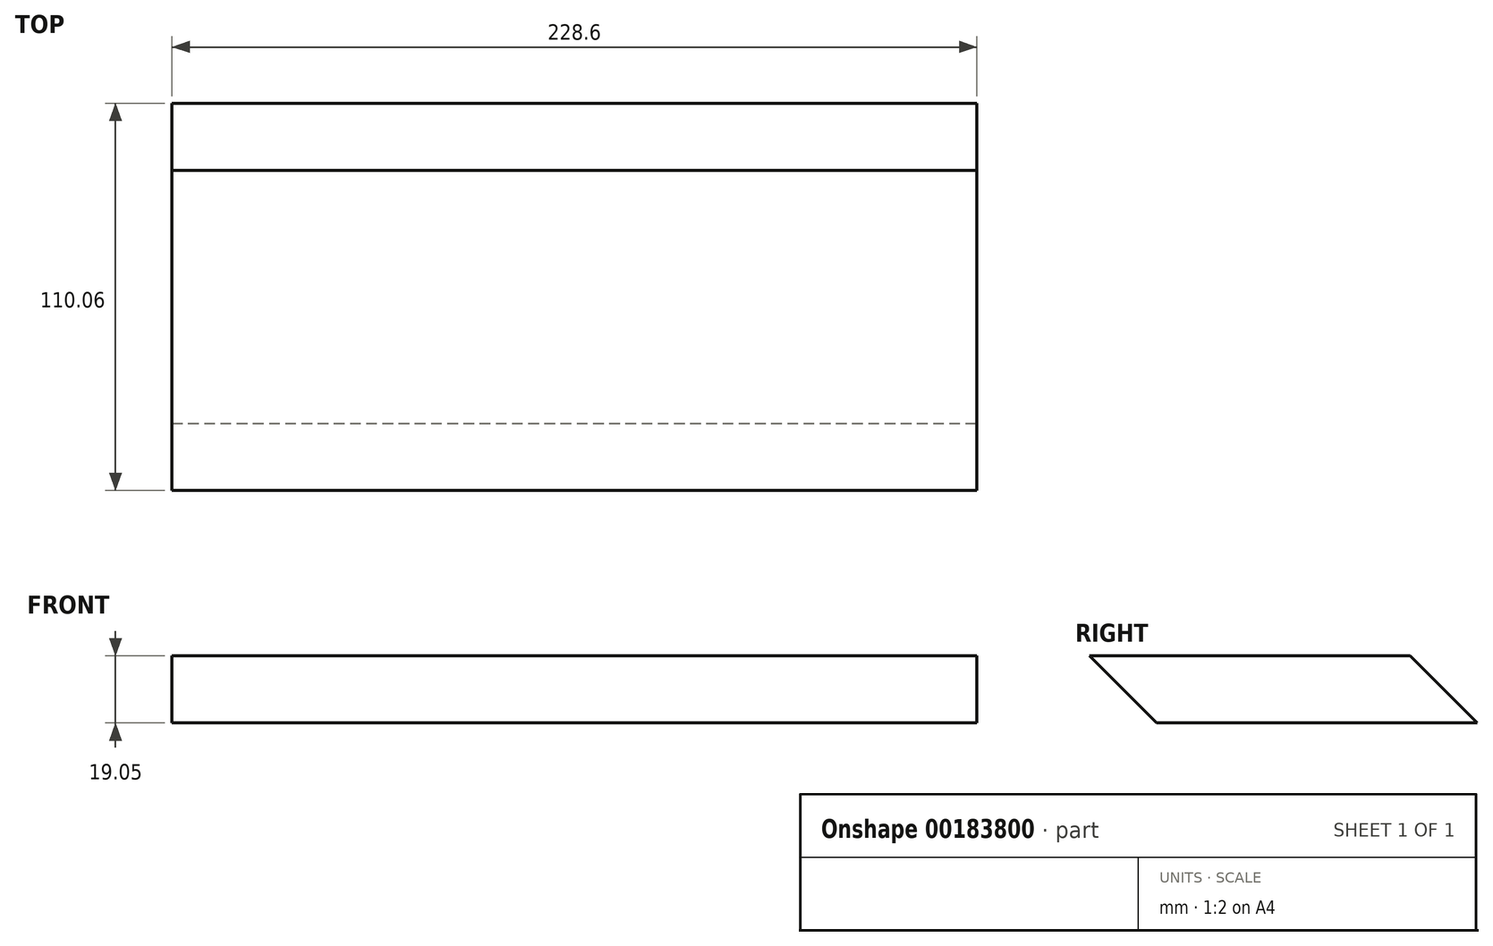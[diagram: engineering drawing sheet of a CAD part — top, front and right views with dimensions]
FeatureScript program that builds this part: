
annotation { "Feature Type Name" : "Feature", "Feature Type Description" : "" }
export const myFeature = defineFeature(function(context is Context, id is Id, definition is map)
    precondition{}
    {
        {
            var Q0;
            Q0=qCreatedBy(makeId("Right.planeOp"),FACE);
            var sketch = newSketch(context, id + "F0", { "sketchPlane" : qUnion([Q0])});
            skLineSegment(sketch, "E0.bottom", {"start": v(0, 0) * mm, "end": v(273.05, 0) * mm});
            skLineSegment(sketch, "E0.top", {"start": v(0, 228.6) * mm, "end": v(273.05, 228.6) * mm});
            skLineSegment(sketch, "E0.left", {"start": v(0, 0) * mm, "end": v(0, 228.6) * mm});
            skLineSegment(sketch, "E0.right", {"start": v(273.05, 0) * mm, "end": v(273.05, 228.6) * mm});
            skSolve(sketch);
        }
        {
            var Q0;
            Q0=qSketchRegion(id+"F0",true);
            extrude(context, id + "F1", {"entities" : qUnion([Q0]), "oppositeDirection" : true, "depth" : 228.6 * mm});
        }
        {
            var Q0;
            Q0=makeQuery(id+"F1.opExtrude","CAP_FACE",FACE,{"disambiguationData":[OSD([sQuery(id+"F0.wireOp",EDGE,"E0.bottom"),sQuery(id+"F0.wireOp",EDGE,"E0.top"),sQuery(id+"F0.wireOp",EDGE,"E0.left"),sQuery(id+"F0.wireOp",EDGE,"E0.right")])],"isStart":true});
            var sketch = newSketch(context, id + "F2", { "sketchPlane" : qUnion([Q0])});
            skLineSegment(sketch, "E1", {"start": v(91.02, 228.6) * mm, "end": v(91.02, 69.85) * mm, "construction": true});
            skLineSegment(sketch, "E2", {"start": v(182.03, 228.6) * mm, "end": v(182.03, 139.7) * mm, "construction": true});
            skLineSegment(sketch, "E3", {"start": v(0, 190.24) * mm, "end": v(91.02, 190.24) * mm, "construction": true});
            skLineSegment(sketch, "E4", {"start": v(91.02, 190.24) * mm, "end": v(182.03, 190.24) * mm, "construction": true});
            skLineSegment(sketch, "E5", {"start": v(182.03, 190.24) * mm, "end": v(273.05, 190.24) * mm, "construction": true});
            skLineSegment(sketch, "E6", {"start": v(273.05, 139.7) * mm, "end": v(182.03, 139.7) * mm});
            skLineSegment(sketch, "E7", {"start": v(273.05, 69.85) * mm, "end": v(91.02, 69.85) * mm});
            skLineSegment(sketch, "E8", {"start": v(40.37, 139.7) * mm, "end": v(40.37, 69.85) * mm, "construction": true});
            skLineSegment(sketch, "E9", {"start": v(40.37, 69.85) * mm, "end": v(40.37, 0) * mm, "construction": true});
            skLineSegment(sketch, "E10", {"start": v(91.02, 69.85) * mm, "end": v(91.02, 0) * mm});
            skLineSegment(sketch, "E11", {"start": v(91.02, 69.85) * mm, "end": v(0, 69.85) * mm, "construction": true});
            skLineSegment(sketch, "E12", {"start": v(182.03, 139.7) * mm, "end": v(182.03, 0) * mm});
            skLineSegment(sketch, "E13", {"start": v(182.03, 139.7) * mm, "end": v(0, 139.7) * mm, "construction": true});
            skSolve(sketch);
        }
        {
            var Q0;
            {var subQ1=sQuery(id+"F2.wireOp",EDGE,"E6");Q0=makeQuery(id+"F2.imprint","IMPRINT",FACE,{"disambiguationData":[TD([[makeQuery(id+"F2.imprint","IMPRINT",EDGE,{"derivedFrom":subQ1}),-1.0]])]});}
            var Q1;
            Q1=makeQuery(id+"F1.opExtrude","CAP_FACE",FACE,{"disambiguationData":[OSD([sQuery(id+"F0.wireOp",EDGE,"E0.bottom"),sQuery(id+"F0.wireOp",EDGE,"E0.top"),sQuery(id+"F0.wireOp",EDGE,"E0.left"),sQuery(id+"F0.wireOp",EDGE,"E0.right")])],"isStart":false});
            extrude(context, id + "F3", {"entities" : qUnion([Q0]), "operationType" : NewBodyOperationType.REMOVE, "endBound" : BoundingType.UP_TO_SURFACE, "oppositeDirection" : true, "endBoundEntityFace" : qUnion([Q1]), "depth" : 25.4 * mm});
        }
        {
            var Q0;
            Q0=makeQuery(id+"F1.opExtrude","CAP_FACE",FACE,{"disambiguationData":[OSD([sQuery(id+"F0.wireOp",EDGE,"E0.bottom"),sQuery(id+"F0.wireOp",EDGE,"E0.top"),sQuery(id+"F0.wireOp",EDGE,"E0.left"),sQuery(id+"F0.wireOp",EDGE,"E0.right")])],"isStart":true});
            var sketch = newSketch(context, id + "F4", { "sketchPlane" : qUnion([Q0])});
            skLineSegment(sketch, "E14.0", {"start": v(110.07, 50.8) * mm, "end": v(110.07, 0) * mm});
            skLineSegment(sketch, "E14.1", {"start": v(201.08, 50.8) * mm, "end": v(110.07, 50.8) * mm});
            skLineSegment(sketch, "E14.2", {"start": v(201.08, 120.65) * mm, "end": v(201.08, 50.8) * mm});
            skLineSegment(sketch, "E14.3", {"start": v(273.05, 120.65) * mm, "end": v(201.08, 120.65) * mm});
            skSolve(sketch);
        }
        {
            var Q0;
            {var subQ1=sQuery(id+"F4.wireOp",EDGE,"E14.0");Q0=makeQuery(id+"F4.imprint","IMPRINT",FACE,{"disambiguationData":[TD([[makeQuery(id+"F4.imprint","IMPRINT",EDGE,{"derivedFrom":subQ1}),1.0]])]});}
            extrude(context, id + "F5", {"entities" : qUnion([Q0]), "operationType" : NewBodyOperationType.REMOVE, "endBound" : BoundingType.UP_TO_NEXT, "oppositeDirection" : true, "depth" : 25.4 * mm});
        }
        {
            var Q0;
            Q0=makeQuery(id+"F1.opExtrude","CAP_FACE",FACE,{"disambiguationData":[OSD([sQuery(id+"F0.wireOp",EDGE,"E0.bottom"),sQuery(id+"F0.wireOp",EDGE,"E0.top"),sQuery(id+"F0.wireOp",EDGE,"E0.left"),sQuery(id+"F0.wireOp",EDGE,"E0.right")])],"isStart":true});
            var sketch = newSketch(context, id + "F6", { "sketchPlane" : qUnion([Q0])});
            skLineSegment(sketch, "E15", {"start": v(91.02, 69.85) * mm, "end": v(110.07, 50.8) * mm});
            skLineSegment(sketch, "E16", {"start": v(182.03, 69.85) * mm, "end": v(201.08, 50.8) * mm});
            skLineSegment(sketch, "E17", {"start": v(182.03, 139.7) * mm, "end": v(201.08, 120.65) * mm});
            skSolve(sketch);
        }
        {
            var Q0;
            Q0=makeQuery(id+"F6.imprint","IMPRINT",FACE,{"disambiguationData":[TD([[makeQuery(id+"F6.imprint","IMPRINT",EDGE,{"derivedFrom":sQuery(id+"F6.wireOp",EDGE,"E17")}),1.0]])]});
            var Q1;
            Q1=makeQuery(id+"F6.imprint","IMPRINT",FACE,{"disambiguationData":[TD([[makeQuery(id+"F6.imprint","IMPRINT",EDGE,{"derivedFrom":sQuery(id+"F6.wireOp",EDGE,"E16")}),1.0]])]});
            var Q2;
            Q2=makeQuery(id+"F6.imprint","IMPRINT",FACE,{"disambiguationData":[TD([[makeQuery(id+"F6.imprint","IMPRINT",EDGE,{"derivedFrom":sQuery(id+"F6.wireOp",EDGE,"E15")}),-1.0]])]});
            extrude(context, id + "F7", {"entities" : qUnion([Q0, Q1, Q2]), "operationType" : NewBodyOperationType.REMOVE, "endBound" : BoundingType.UP_TO_NEXT, "oppositeDirection" : true, "depth" : 25.4 * mm});
        }
    });
